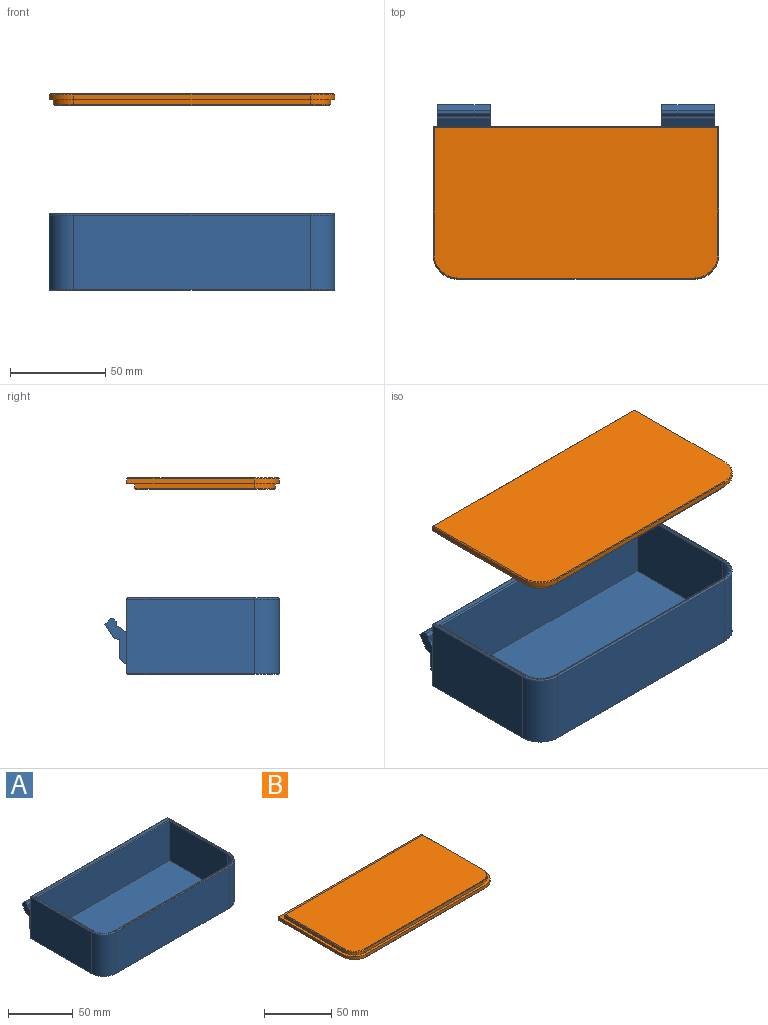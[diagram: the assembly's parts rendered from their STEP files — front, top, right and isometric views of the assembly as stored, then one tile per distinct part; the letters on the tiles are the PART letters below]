
ASSEMBLY  parts=2 mates=1
PART A: 57 faces, bbox 152.1x92.7x40 mm
  f0: plane 150x39mm, normal (0,1,0), area 4924mm2, adj f2,f4,f17,f18,f23,f24,f28,f29
  f1: plane 148.5x78.5mm, normal (0,0,1), area 515.8mm2, adj f39,f40,f41,f42,f43,f44,f45,f46
  f2: plane 67x39mm, normal (-1,0,0), area 2613mm2, adj f0,f12,f48,f52
  f3: plane 124x39mm, normal (0,-1,0), area 4836mm2, adj f12,f13,f49,f53
  f4: plane 67x39mm, normal (1,0,0), area 2613mm2, adj f0,f13,f45,f56
  f5: plane 149.5x79.5mm, normal (0,0,-1), area 11815.5mm2, adj f51,f52,f53,f54,f55,f56
  f6: plane 63x37.25mm, normal (1,0,0), area 2346.7mm2, adj f9,f11,f36,f42
  f7: plane 124x37.25mm, normal (0,1,0), area 4619mm2, adj f9,f10,f11,f39
  f8: plane 63x37.25mm, normal (-1,0,0), area 2346.7mm2, adj f9,f10,f36,f43
  f9: plane 146x74mm, normal (0,0,1), area 10752.1mm2, adj f6,f7,f8,f10,f11,f36
  f10: cylinder r=11mm len=37.25mm, axis (0,0,-1), area 643.6mm2, adj f7,f8,f9,f41
  f11: cylinder r=11mm len=37.25mm, axis (0,0,1), area 643.6mm2, adj f6,f7,f9,f40
  f12: cylinder r=13mm len=39mm, axis (0,0,-1), area 796.4mm2, adj f2,f3,f50,f51
  f13: cylinder r=13mm len=39mm, axis (0,0,1), area 796.4mm2, adj f3,f4,f47,f55
  f14: plane 27.7x1.48mm, normal (0,0,1), area 41mm2, adj f22,f23,f24,f37
  f15: plane 27.7x2.65mm, normal (0,-1,0), area 73.4mm2, adj f16,f23,f24,f37
  f16: plane 27.7x1.01mm, normal (0,0,1), area 28mm2, adj f15,f17,f23,f24
  f17: plane 27.7x4.57mm, normal (0,-0.59,0.81), area 157.1mm2, adj f0,f16,f23,f24
  f18: plane 27.7x3.68mm, normal (0,0.63,-0.78), area 130.6mm2, adj f0,f19,f23,f24
  f19: plane 27.7x10mm, normal (0,1,0), area 277mm2, adj f18,f20,f23,f24
  f20: plane 27.7x3.37mm, normal (0,0.32,-0.95), area 98.3mm2, adj f19,f21,f23,f24
  f21: plane 27.7x7.02mm, normal (0,0.83,-0.55), area 233mm2, adj f20,f22,f23,f24
  f22: plane 27.7x3.12mm, normal (0,0.71,0.71), area 122.2mm2, adj f14,f21,f23,f24
  f23: plane 24.22x11.68mm, normal (-1,0,0), area 113.6mm2, adj f0,f14,f15,f16,f17,f18,f19,f20
  f24: plane 24.22x11.68mm, normal (1,0,0), area 113.6mm2, adj f0,f14,f15,f16,f17,f18,f19,f20
  f25: plane 27.7x1.48mm, normal (0,0,1), area 41mm2, adj f33,f34,f35,f38
  f26: plane 27.7x2.65mm, normal (0,-1,0), area 73.4mm2, adj f27,f34,f35,f38
  f27: plane 27.7x1.01mm, normal (0,0,1), area 28mm2, adj f26,f28,f34,f35
  f28: plane 27.7x4.57mm, normal (0,-0.59,0.81), area 157.1mm2, adj f0,f27,f34,f35
  f29: plane 27.7x3.68mm, normal (0,0.63,-0.78), area 130.6mm2, adj f0,f30,f34,f35
  f30: plane 27.7x10mm, normal (0,1,0), area 277mm2, adj f29,f31,f34,f35
  f31: plane 27.7x3.37mm, normal (0,0.32,-0.95), area 98.3mm2, adj f30,f32,f34,f35
  f32: plane 27.7x7.02mm, normal (0,0.83,-0.55), area 233mm2, adj f31,f33,f34,f35
  f33: plane 27.7x3.12mm, normal (0,0.71,0.71), area 122.2mm2, adj f25,f32,f34,f35
  f34: plane 24.22x11.68mm, normal (1,0,0), area 113.6mm2, adj f0,f25,f26,f27,f28,f29,f30,f31
  f35: plane 24.22x11.68mm, normal (-1,0,0), area 113.6mm2, adj f0,f25,f26,f27,f28,f29,f30,f31
  f36: plane 146x37.25mm, normal (0,-1,0), area 5438.5mm2, adj f6,f8,f9,f44
  f37: plane 27.7x1.5mm, normal (0,-0.71,0.71), area 58.8mm2, adj f14,f15,f23,f24
  f38: plane 27.7x1.5mm, normal (0,-0.71,0.71), area 58.8mm2, adj f25,f26,f34,f35
  f39: cylinder r=0.75mm len=124mm, axis (1,0,0), area 146.1mm2, adj f1,f7,f40,f41
  f40: torus R=11.75mm, axis (0,0,1), area 20.9mm2, adj f1,f11,f39,f42
  f41: torus R=11.75mm, axis (0,0,1), area 20.9mm2, adj f1,f10,f39,f43
  f42: cylinder r=0.75mm len=63.75mm, axis (0,-1,0), area 74.5mm2, adj f1,f6,f40,f44
  f43: cylinder r=0.75mm len=63.75mm, axis (0,1,0), area 74.5mm2, adj f1,f8,f41,f44
  f44: cylinder r=0.75mm len=147.5mm, axis (-1,0,0), area 172.6mm2, adj f1,f36,f42,f43
  f45: cylinder r=0.75mm len=67mm, axis (0,-1,0), area 78.6mm2, adj f1,f4,f46,f47
  f46: cylinder r=0.75mm len=150mm, axis (1,0,0), area 176.1mm2, adj f0,f1,f45,f48
  f47: torus R=12.25mm, axis (0,0,1), area 23.6mm2, adj f1,f13,f45,f49
  f48: cylinder r=0.75mm len=67mm, axis (0,1,0), area 78.6mm2, adj f1,f2,f46,f50
  f49: cylinder r=0.75mm len=124mm, axis (-1,0,0), area 146.1mm2, adj f1,f3,f47,f50
  f50: torus R=12.25mm, axis (0,0,1), area 23.6mm2, adj f1,f12,f48,f49
  f51: cone r=12.75mm half-angle=45deg, axis (0,0,1), area 7.2mm2, adj f5,f12,f52,f53
  f52: plane 67x0.25mm, normal (-0.71,0,-0.71), area 23.6mm2, adj f2,f5,f51,f54
  f53: plane 124x0.25mm, normal (0,-0.71,-0.71), area 43.8mm2, adj f3,f5,f51,f55
  f54: plane 150x0.25mm, normal (0,0.71,-0.71), area 52.9mm2, adj f0,f5,f52,f56
  f55: cone r=12.75mm half-angle=45deg, axis (0,0,1), area 7.2mm2, adj f5,f13,f53,f56
  f56: plane 67x0.25mm, normal (0.71,0,-0.71), area 23.6mm2, adj f4,f5,f54,f55
PART B: 27 faces, bbox 150x80x6 mm
  f0: plane 150x80mm, normal (0,0,1), area 1250.5mm2, adj f1,f2,f3,f4,f6,f7,f9,f10
  f1: plane 150x2.5mm, normal (0,1,0), area 375mm2, adj f0,f2,f4,f24
  f2: plane 67x2.5mm, normal (-1,0,0), area 167.5mm2, adj f0,f1,f6,f22
  f3: plane 124x2.5mm, normal (0,-1,0), area 310mm2, adj f0,f6,f7,f23
  f4: plane 67x2.5mm, normal (1,0,0), area 167.5mm2, adj f0,f1,f7,f26
  f5: plane 149x79mm, normal (0,0,-1), area 11703.9mm2, adj f21,f22,f23,f24,f25,f26
  f6: cylinder r=13mm len=13mm, axis (0,0,1), area 51.1mm2, adj f0,f2,f3,f21
  f7: cylinder r=13mm len=13mm, axis (0,0,-1), area 51.1mm2, adj f0,f3,f4,f25
  f8: plane 144.48x72.48mm, normal (0,0,1), area 10426mm2, adj f15,f16,f17,f18,f19,f20
  f9: plane 124x2.52mm, normal (0,-1,0.03), area 312.4mm2, adj f0,f10,f11,f15
  f10: cone r=10.72mm half-angle=2deg, axis (0,0,-1), area 42.7mm2, adj f0,f9,f12,f17
  f11: cone r=10.72mm half-angle=2deg, axis (0,0,-1), area 42.7mm2, adj f0,f9,f13,f16
  f12: plane 62.83x2.52mm, normal (-1,0,0.03), area 158.1mm2, adj f0,f10,f14,f19
  f13: plane 62.83x2.52mm, normal (1,0,0.03), area 158.1mm2, adj f0,f11,f14,f18
  f14: plane 145.65x2.52mm, normal (0,1,0.03), area 366.7mm2, adj f0,f12,f13,f20
  f15: plane 124x0.5mm, normal (0,-0.69,0.72), area 86.1mm2, adj f8,f9,f16,f17
  f16: cone r=10.24mm half-angle=46deg, axis (0,0,-1), area 11.4mm2, adj f8,f11,f15,f18
  f17: cone r=10.24mm half-angle=46deg, axis (0,0,-1), area 11.4mm2, adj f8,f10,f15,f19
  f18: plane 62.74x0.5mm, normal (0.69,0,0.72), area 43.4mm2, adj f8,f13,f16,f20
  f19: plane 62.74x0.5mm, normal (-0.69,0,0.72), area 43.4mm2, adj f8,f12,f17,f20
  f20: plane 145.48x0.5mm, normal (0,0.69,0.72), area 100.7mm2, adj f8,f14,f18,f19
  f21: cone r=12.5mm half-angle=45deg, axis (0,0,1), area 14.2mm2, adj f5,f6,f22,f23
  f22: plane 67x0.5mm, normal (-0.71,0,-0.71), area 47.2mm2, adj f2,f5,f21,f24
  f23: plane 124x0.5mm, normal (0,-0.71,-0.71), area 87.7mm2, adj f3,f5,f21,f25
  f24: plane 150x0.5mm, normal (0,0.71,-0.71), area 105.7mm2, adj f1,f5,f22,f26
  f25: cone r=12.5mm half-angle=45deg, axis (0,0,1), area 14.2mm2, adj f5,f7,f23,f26
  f26: plane 67x0.5mm, normal (0.71,0,-0.71), area 47.2mm2, adj f4,f5,f24,f25
PLACE A t=(-20.93,-2.14,3.67)mm fixed
PLACE B rot(axis=(0,1,0),180deg) t=(-20.93,-2.12,6.52)mm
MATE slider A.f9 <-> B.f8  axis (0,0,1) through (-20.93,-2.98,5.67)mm
